# Revit family: FTT
name_source: partatom
category: Generic Models
revit_build: Autodesk Revit 2017 (Build: 20190508_0315(x64)
units: mm (PartAtom-declared; Revit-internal decimal feet)

## family parameters
Always vertical = Yes
Can host rebar = No
Cut with Voids When Loaded = No
Part Type = Normal
Room Calculation Point = No
Round Connector Dimension = Use Diameter
Shared = Yes
Work Plane-Based = No

## types (19) — shared parameters

## per-type parameters (varying)
| type | # OF HOLES | Trak Length |
| FTT-200 | 2 | 200 mm  [stored 0.656168 ft] |
| FTT-300 | 4 | 300 mm |
| FTT-400 | 6 | 400 mm  [stored 1.31234 ft] |
| FTT-500 | 8 | 500 mm  [stored 1.64042 ft] |
| FTT-600 | 10 | 600 mm |
| FTT-700 | 12 | 700 mm  [stored 2.29659 ft] |
| FTT-800 | 14 | 800 mm  [stored 2.62467 ft] |
| FTT-900 | 16 | 900 mm  [stored 2.95276 ft] |
| FTT-1000 | 18 | 1000 mm  [stored 3.28084 ft] |
| FTT-1100 | 20 | 1100 mm |
| FTT-1200 | 22 | 1200 mm |
| FTT-1300 | 24 | 1300 mm  [stored 4.26509 ft] |
| FTT-1400 | 26 | 1400 mm  [stored 4.59318 ft] |
| FTT-1500 | 28 | 1500 mm  [stored 4.92126 ft] |
| FTT-1600 | 30 | 1600 mm  [stored 5.24934 ft] |
| FTT-1700 | 32 | 1700 mm  [stored 5.57743 ft] |
| FTT-1800 | 34 | 1800 mm  [stored 5.90551 ft] |
| FTT-1900 | 36 | 1900 mm  [stored 6.2336 ft] |
| FTT-2000 | 38 | 2000 mm  [stored 6.56168 ft] |

note: [stored X ft] marks values corroborated as IEEE doubles in the binary element streams (Revit-internal decimal feet)

## geometry (parser evidence)
native form markers: Sweep x5
no freeform markers — native parametric forms only
